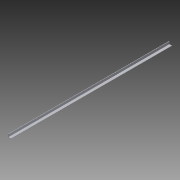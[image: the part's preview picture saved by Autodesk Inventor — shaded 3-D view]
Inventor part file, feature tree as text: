
AUTODESK INVENTOR PART (.ipt)
format: ipt  version: 2014 SP1 (Build 180222100, 222)  size: 75,264 bytes
history: native  units: in
note: dims shown in document units (in); Inventor stores cm internally (conversion verified against a paired STEP export)
features: extrude x1, sketch x1
ambient origin geometry x8: Origin, YZ Plane, XZ Plane, XY Plane, X Axis, Y Axis, Z Axis, Center Point
bodies: Solid1 (feature_tree)
feature tree (2):
  extrude  "Extrusion1"  Depth=0.0625in
  sketch  "Sketch1"  dims[d0=0.5in d1=0.0625in d2=0.5in d3=0.0625in d4=27.25in d5=0.0in]
